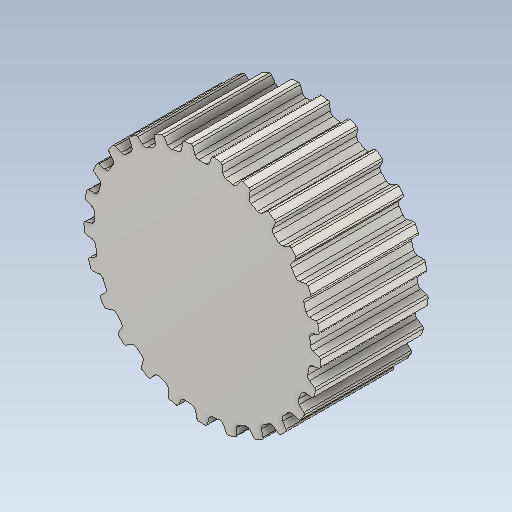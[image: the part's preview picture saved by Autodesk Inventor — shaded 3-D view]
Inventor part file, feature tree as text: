
AUTODESK INVENTOR PART (.ipt)
format: ipt  version: 2020 (Build 240168000, 168)  size: 365,568 bytes
history: native  units: mm (DEFAULTED — no unit token found)
features: other x3, extrude x2, fillet x1, pattern_circular x1
ambient origin geometry x8: Origin, YZ Plane, XZ Plane, XY Plane, X Axis, Y Axis, Z Axis, Center Point
bodies: Solid1 (feature_tree)
feature tree (7):
  other  "Pulley Sketch"
  extrude  "Base Body"  Depth=16.170142mm
  extrude  "Tooth"  Depth=0.254mm
  fillet  "Tooth Fillet"  Radius=0.6858mm
  pattern_circular  "Teeth"  [2 undecoded]
  other  "Left flange"
  other  "Right flange"
note: 2 required parameter values undecoded (feature->parameter linkage not recoverable at this tier; creation-order binding heuristic only, values carry confidence <= 0.55)
